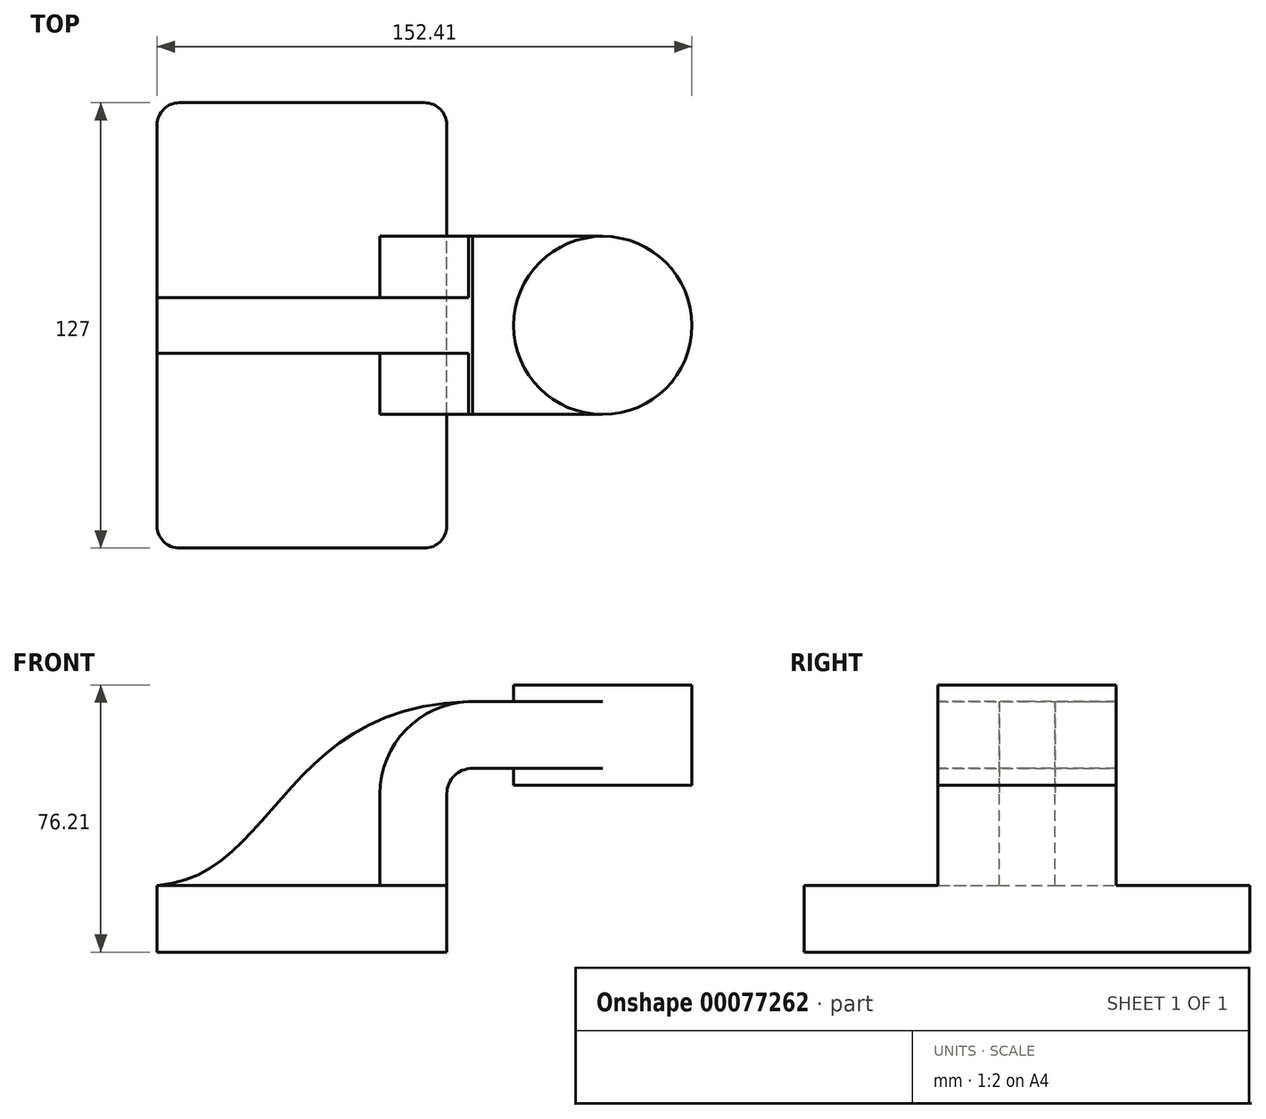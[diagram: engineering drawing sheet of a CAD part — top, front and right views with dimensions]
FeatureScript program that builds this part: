
annotation { "Feature Type Name" : "Feature", "Feature Type Description" : "" }
export const myFeature = defineFeature(function(context is Context, id is Id, definition is map)
    precondition{}
    {
        {
            var Q0;
            Q0=qCreatedBy(makeId("Front.planeOp"),FACE);
            var sketch = newSketch(context, id + "F0", { "sketchPlane" : qUnion([Q0])});
            skLineSegment(sketch, "E0.bottom", {"start": v(41.27, 9.53) * mm, "end": v(-41.28, 9.53) * mm});
            skLineSegment(sketch, "E0.top", {"start": v(41.28, -9.52) * mm, "end": v(-41.27, -9.52) * mm});
            skLineSegment(sketch, "E0.left", {"start": v(41.28, 9.53) * mm, "end": v(41.28, -9.52) * mm});
            skLineSegment(sketch, "E0.right", {"start": v(-41.28, 9.53) * mm, "end": v(-41.27, -9.52) * mm});
            skPoint(sketch, "E0.middle", {"position": v(0, 0) * mm});
            skLineSegment(sketch, "E1.bottom", {"start": v(111.13, 38.1) * mm, "end": v(60.33, 38.1) * mm});
            skLineSegment(sketch, "E1.top", {"start": v(111.13, 66.68) * mm, "end": v(60.33, 66.68) * mm});
            skLineSegment(sketch, "E1.left", {"start": v(111.13, 38.1) * mm, "end": v(111.13, 66.68) * mm});
            skLineSegment(sketch, "E1.right", {"start": v(60.33, 38.1) * mm, "end": v(60.33, 66.68) * mm});
            skPoint(sketch, "E1.middle", {"position": v(85.73, 52.39) * mm});
            skPoint(sketch, "E2.endSnap0", {"position": v(60.33, 52.39) * mm});
            skLineSegment(sketch, "E3", {"start": v(41.27, 9.53) * mm, "end": v(41.27, 35.6) * mm});
            skArc(sketch, "E4", {"start": v(41.27, 35.6) * mm, "mid": v(43.4, 40.74) * mm, "end": v(48.55, 42.88) * mm});
            skLineSegment(sketch, "E5", {"start": v(48.55, 42.88) * mm, "end": v(85.73, 42.88) * mm});
            skLineSegment(sketch, "E6.0", {"start": v(48.55, 61.93) * mm, "end": v(85.73, 61.93) * mm});
            skArc(sketch, "E6.1", {"start": v(22.22, 35.6) * mm, "mid": v(29.94, 54.21) * mm, "end": v(48.55, 61.93) * mm});
            skLineSegment(sketch, "E6.2", {"start": v(22.22, 9.53) * mm, "end": v(22.22, 35.6) * mm});
            skLineSegment(sketch, "E7", {"start": v(85.73, 38.1) * mm, "end": v(85.73, 66.68) * mm});
            skFitSpline(sketch, "E8", {"points": [v(-41.28, 9.53) * mm, v(48.55, 61.93) * mm], "startDerivative": vector(102.12, 6.96) * mm, "endDerivative": vector(164.03, 2.52) * mm});
            skSolve(sketch);
        }
        {
            var Q0;
            Q0=makeQuery(id+"F0.imprint","IMPRINT",FACE,{"disambiguationData":[TD([[makeQuery(id+"F0.imprint","IMPRINT",EDGE,{"derivedFrom":sQuery(id+"F0.wireOp",EDGE,"E0.top")}),-1.0]])]});
            extrude(context, id + "F1", {"entities" : qUnion([Q0]), "endBound" : BoundingType.SYMMETRIC, "depth" : 127 * mm});
        }
        {
            var Q0;
            {var subQ1=sQuery(id+"F0.wireOp",EDGE,"E3");Q0=makeQuery(id+"F0.imprint","IMPRINT",FACE,{"disambiguationData":[TD([[makeQuery(id+"F0.imprint","IMPRINT",EDGE,{"derivedFrom":subQ1}),1.0]])]});}
            var Q1;
            {var subQ0=sQuery(id+"F0.wireOp",EDGE,"E5");var subQ1=sQuery(id+"F0.wireOp",EDGE,"E1.right");var subQ2=makeQuery(id+"F0.imprint","INTERSECT",VERTEX,{"derivedFrom":[subQ1,subQ0]});Q1=makeQuery(id+"F0.imprint","IMPRINT",FACE,{"disambiguationData":[TD([[makeQuery(id+"F0.imprint","IMPRINT",EDGE,{"disambiguationData":[TD([[subQ2,-1.0]])],"derivedFrom":subQ1}),-1.0]])]});}
            extrude(context, id + "F2", {"entities" : qUnion([Q0, Q1]), "operationType" : NewBodyOperationType.ADD, "endBound" : BoundingType.SYMMETRIC, "depth" : 50.8 * mm});
        }
        {
            var Q0;
            {var subQ3=sQuery(id+"F0.wireOp",EDGE,"E6.2");Q0=makeQuery(id+"F0.imprint","IMPRINT",FACE,{"disambiguationData":[TD([[makeQuery(id+"F0.imprint","IMPRINT",EDGE,{"derivedFrom":subQ3}),1.0]])]});}
            extrude(context, id + "F3", {"entities" : qUnion([Q0]), "operationType" : NewBodyOperationType.ADD, "endBound" : BoundingType.SYMMETRIC, "depth" : 15.88 * mm});
        }
        {
            var Q0;
            {var subQ0=sQuery(id+"F0.wireOp",EDGE,"E1.left");Q0=makeQuery(id+"F0.imprint","IMPRINT",FACE,{"disambiguationData":[TD([[makeQuery(id+"F0.imprint","IMPRINT",EDGE,{"derivedFrom":subQ0}),1.0]])]});}
            var Q1;
            Q1=sQuery(id+"F0.wireOp",EDGE,"E7");
            revolve(context, id + "F4", {"operationType" : NewBodyOperationType.ADD, "entities" : qUnion([Q0]), "axis" : qUnion([Q1]), "revolveType" : RevolveType.FULL});
        }
        {
            var Q0;
            Q0=makeQuery(id+"F1.opExtrude","CAP_EDGE",EDGE,{"disambiguationData":[OSD([sQuery(id+"F0.wireOp",EDGE,"E0.left")])],"isStart":false});
            var Q1;
            Q1=makeQuery(id+"F1.opExtrude","CAP_EDGE",EDGE,{"disambiguationData":[OSD([sQuery(id+"F0.wireOp",EDGE,"E0.right")])],"isStart":false});
            var Q2;
            Q2=makeQuery(id+"F1.opExtrude","CAP_EDGE",EDGE,{"disambiguationData":[OSD([sQuery(id+"F0.wireOp",EDGE,"E0.left")])],"isStart":true});
            var Q3;
            Q3=makeQuery(id+"F1.opExtrude","CAP_EDGE",EDGE,{"disambiguationData":[OSD([sQuery(id+"F0.wireOp",EDGE,"E0.right")])],"isStart":true});
            fillet(context, id + "F5", {"entities" : qUnion([Q0, Q1, Q2, Q3]), "radius" : 6.35 * mm, "tangentPropagation" : true, "allowEdgeOverflow" : false});
        }
    });
